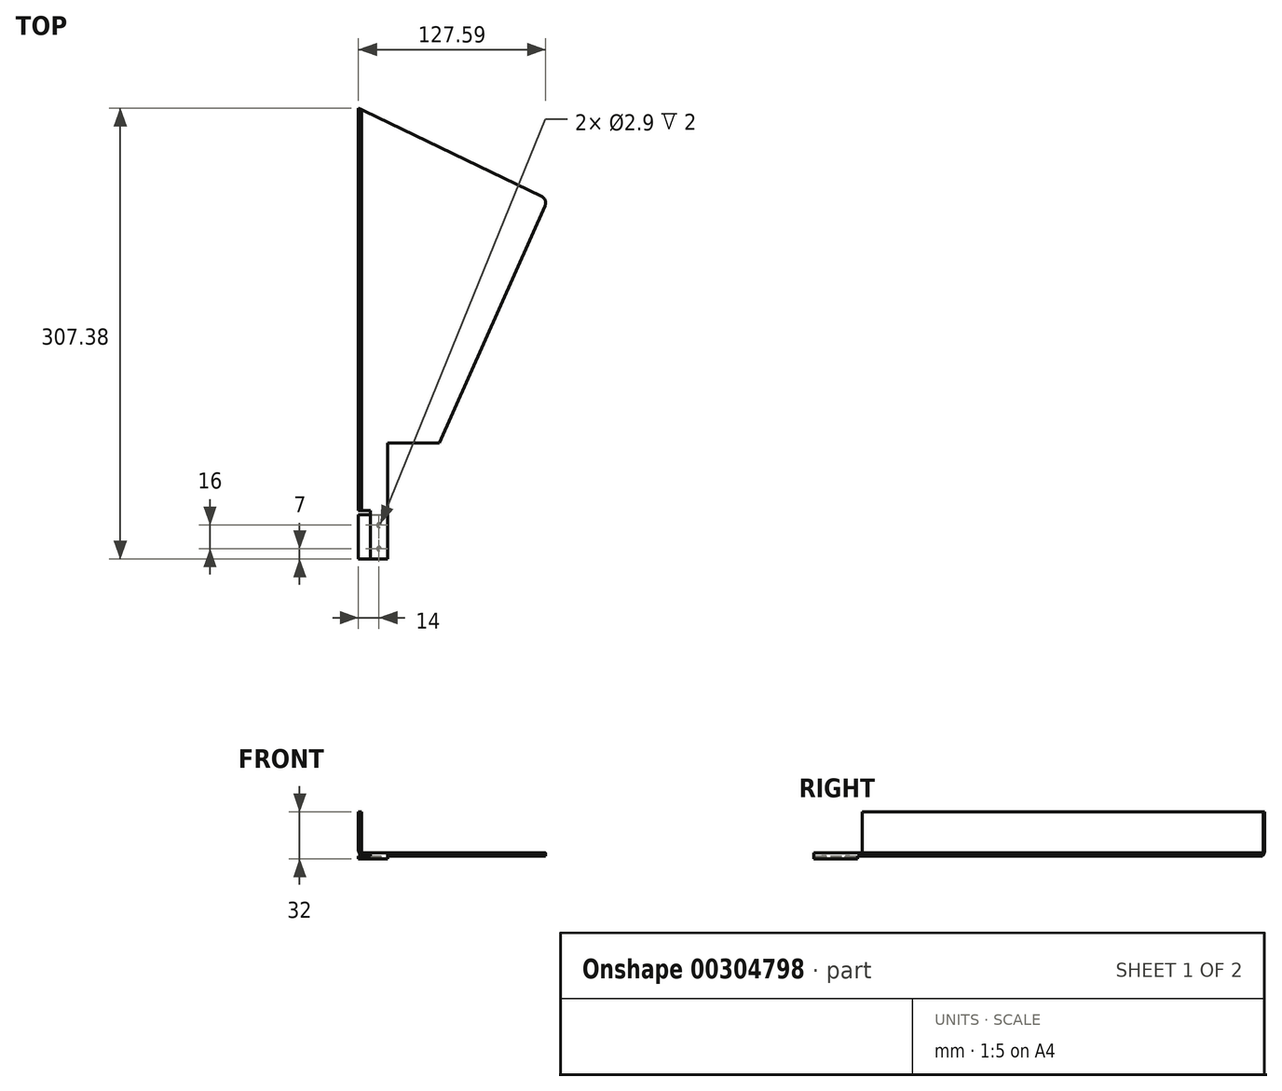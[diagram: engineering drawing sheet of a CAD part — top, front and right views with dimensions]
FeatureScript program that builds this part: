
annotation { "Feature Type Name" : "Feature", "Feature Type Description" : "" }
export const myFeature = defineFeature(function(context is Context, id is Id, definition is map)
    precondition{}
    {
        {
            var Q0;
            Q0=qCreatedBy(makeId("Front.planeOp"),FACE);
            var sketch = newSketch(context, id + "F0", { "sketchPlane" : qUnion([Q0])});
            skLineSegment(sketch, "E0", {"start": v(-22.5, 28) * mm, "end": v(-22.5, 2) * mm});
            skLineSegment(sketch, "E1", {"start": v(-20.5, 0) * mm, "end": v(125.5, 0) * mm});
            skPoint(sketch, "E2", {"position": v(0, 0) * mm});
            skPoint(sketch, "E3.visualSharp", {"position": v(-22.5, 0) * mm});
            skArc(sketch, "E3.filletArc", {"start": v(-22.5, 2) * mm, "mid": v(-21.91, 0.59) * mm, "end": v(-20.5, 0) * mm});
            skLineSegment(sketch, "E4", {"start": v(-22.5, 28) * mm, "end": v(-24.5, 28) * mm});
            skLineSegment(sketch, "E5", {"start": v(-24.5, 28) * mm, "end": v(-24.5, 2) * mm});
            skLineSegment(sketch, "E6", {"start": v(-20.5, -2) * mm, "end": v(125.5, -2) * mm});
            skPoint(sketch, "E7.visualSharp", {"position": v(-24.5, -2) * mm});
            skArc(sketch, "E7.filletArc", {"start": v(-24.5, 2) * mm, "mid": v(-23.33, -0.83) * mm, "end": v(-20.5, -2) * mm});
            skLineSegment(sketch, "E8", {"start": v(125.5, 0) * mm, "end": v(125.5, -2) * mm});
            skSolve(sketch);
        }
        {
            var Q0;
            Q0=qSketchRegion(id+"F0",true);
            extrude(context, id + "F1", {"entities" : qUnion([Q0]), "oppositeDirection" : true, "depth" : 400 * mm});
        }
        {
            var Q0;
            Q0=qCreatedBy(makeId("Top.planeOp"),FACE);
            var sketch = newSketch(context, id + "F2", { "sketchPlane" : qUnion([Q0])});
            skLineSegment(sketch, "E9.bottom", {"start": v(-56.37, 409.92) * mm, "end": v(165.37, 409.92) * mm});
            skLineSegment(sketch, "E9.top", {"start": v(-56.37, -13.1) * mm, "end": v(165.37, -13.1) * mm});
            skLineSegment(sketch, "E9.left", {"start": v(-56.37, 409.92) * mm, "end": v(-56.37, -13.1) * mm});
            skLineSegment(sketch, "E9.right", {"start": v(165.37, 409.92) * mm, "end": v(165.37, -13.1) * mm});
            skLineSegment(sketch, "E10.12.0", {"start": v(-24.5, 307.38) * mm, "end": v(100.26, 247.21) * mm});
            skLineSegment(sketch, "E10.12.1", {"start": v(-24.5, 33) * mm, "end": v(-24.5, 307.38) * mm});
            skLineSegment(sketch, "E10.12.3", {"start": v(30.7, 79.07) * mm, "end": v(102.66, 240.68) * mm});
            skLineSegment(sketch, "E10.12.5", {"start": v(-4.5, 0) * mm, "end": v(-4.5, 79.07) * mm});
            skLineSegment(sketch, "E10.12.6", {"start": v(-4.5, 79.07) * mm, "end": v(30.7, 79.07) * mm});
            skLineSegment(sketch, "E10.12.8", {"start": v(-16.5, 33) * mm, "end": v(-24.5, 33) * mm});
            skLineSegment(sketch, "E10.12.9", {"start": v(-16.5, 33) * mm, "end": v(-16.5, 0) * mm});
            skLineSegment(sketch, "E10.12.10", {"start": v(-16.5, 0) * mm, "end": v(-4.5, 0) * mm});
            skPoint(sketch, "E11.visualSharp", {"position": v(104.63, 245.1) * mm});
            skArc(sketch, "E11.filletArc", {"start": v(102.66, 240.68) * mm, "mid": v(102.78, 244.43) * mm, "end": v(100.26, 247.21) * mm});
            skPoint(sketch, "E12", {"position": v(-24.5, 0) * mm});
            skSolve(sketch);
        }
        {
            var Q0;
            Q0 = qSketchRegion(id + "F2", true);
            extrude(context, id + "F3", {"entities" : qUnion([Q0]), "operationType" : NewBodyOperationType.REMOVE, "endBound" : BoundingType.SYMMETRIC, "oppositeDirection" : true, "depth" : 100 * mm});
        }
        {
            var Q0;
            Q0=makeQuery(id+"F1.opExtrude","SWEPT_FACE",FACE,{"disambiguationData":[OSD([sQuery(id+"F0.wireOp",EDGE,"E6")])]});
            var sketch = newSketch(context, id + "F4", { "sketchPlane" : qUnion([Q0])});
            skCircle(sketch, "E13", {"center": v(-18.5, -7) * mm, "radius": 1.45 * mm});
            skCircle(sketch, "E14", {"center": v(-18.5, -23) * mm, "radius": 1.45 * mm});
            skSolve(sketch);
        }
        {
            var Q0;
            Q0 = qSketchRegion(id + "F4", true);
            extrude(context, id + "F5", {"entities" : qUnion([Q0]), "operationType" : NewBodyOperationType.REMOVE, "oppositeDirection" : true, "depth" : 25 * mm});
        }
        {
            var Q0;
            Q0=makeQuery(id+"F1.opExtrude","SWEPT_FACE",FACE,{"disambiguationData":[OSD([sQuery(id+"F0.wireOp",EDGE,"E6")])]});
            var sketch = newSketch(context, id + "F6", { "sketchPlane" : qUnion([Q0])});
            skLineSegment(sketch, "E15", {"start": v(-16.5, 0) * mm, "end": v(-36.5, 0) * mm});
            skLineSegment(sketch, "E16", {"start": v(-36.5, 0) * mm, "end": v(-36.5, -30) * mm});
            skLineSegment(sketch, "E17", {"start": v(-36.5, -30) * mm, "end": v(-16.5, -30) * mm});
            skLineSegment(sketch, "E18", {"start": v(-16.5, 0) * mm, "end": v(-4.5, 0) * mm});
            skLineSegment(sketch, "E19", {"start": v(-4.5, 0) * mm, "end": v(-4.5, -30) * mm});
            skCircle(sketch, "E20", {"center": v(-30.5, -7) * mm, "radius": 1.45 * mm});
            skCircle(sketch, "E21", {"center": v(-30.5, -23) * mm, "radius": 1.45 * mm});
            skCircle(sketch, "E22", {"center": v(-10.5, -7) * mm, "radius": 1.45 * mm});
            skCircle(sketch, "E23", {"center": v(-10.5, -23) * mm, "radius": 1.45 * mm});
            skLineSegment(sketch, "E24", {"start": v(-4.5, -30) * mm, "end": v(-16.5, -30) * mm});
            skLineSegment(sketch, "E25", {"start": v(-16.5, 0) * mm, "end": v(-16.5, -30) * mm});
            skLineSegment(sketch, "E26", {"start": v(-24.5, 0) * mm, "end": v(-24.5, -30) * mm});
            skSolve(sketch);
        }
        {
            var Q0;
            {var subQ0=sQuery(id+"F6.wireOp",EDGE,"E25");Q0=makeQuery(id+"F6.imprint","IMPRINT",FACE,{"disambiguationData":[TD([[makeQuery(id+"F6.imprint","IMPRINT",EDGE,{"derivedFrom":subQ0}),-1.0]])]});}
            var Q1;
            {var subQ3=sQuery(id+"F6.wireOp",EDGE,"E25");Q1=makeQuery(id+"F6.imprint","IMPRINT",FACE,{"disambiguationData":[TD([[makeQuery(id+"F6.imprint","IMPRINT",EDGE,{"derivedFrom":subQ3}),1.0]])]});}
            var Q2;
            {var subQ6=sQuery(id+"F6.wireOp",EDGE,"E19");Q2=makeQuery(id+"F6.imprint","IMPRINT",FACE,{"disambiguationData":[TD([[makeQuery(id+"F6.imprint","IMPRINT",EDGE,{"derivedFrom":subQ6}),-1.0]])]});}
            extrude(context, id + "F7", {"entities" : qUnion([Q0, Q1, Q2]), "operationType" : NewBodyOperationType.ADD, "depth" : 2 * mm});
        }
    });
